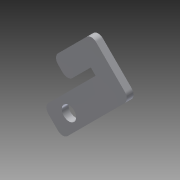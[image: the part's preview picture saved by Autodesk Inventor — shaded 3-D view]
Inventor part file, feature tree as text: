
AUTODESK INVENTOR PART (.ipt)
format: ipt  version: 2014 SP1 (Build 180222100, 222)  size: 111,616 bytes
history: native  units: in
note: dims shown in document units (in); Inventor stores cm internally (conversion verified against a paired STEP export)
features: reference x5, extrude x1, fillet x1, sketch x1
ambient origin geometry x8: Origin, YZ Plane, XZ Plane, XY Plane, X Axis, Y Axis, Z Axis, Center Point
bodies: Solid1 (feature_tree)
feature tree (8):
  extrude  "Extrusion1"  Depth=0.125in
  fillet  "Fillet1"  Radius=1.75in
  sketch  "Sketch1"  dims[d4=0.125in d5=0.0in d6=0.125in d7=1.75in d8=1.0in d9=1.0in d10=0.5in]
  reference  "Reference2"
  reference  "Reference3"
  reference  "Reference4"
  reference  "Reference5"
  reference  "Reference6"
